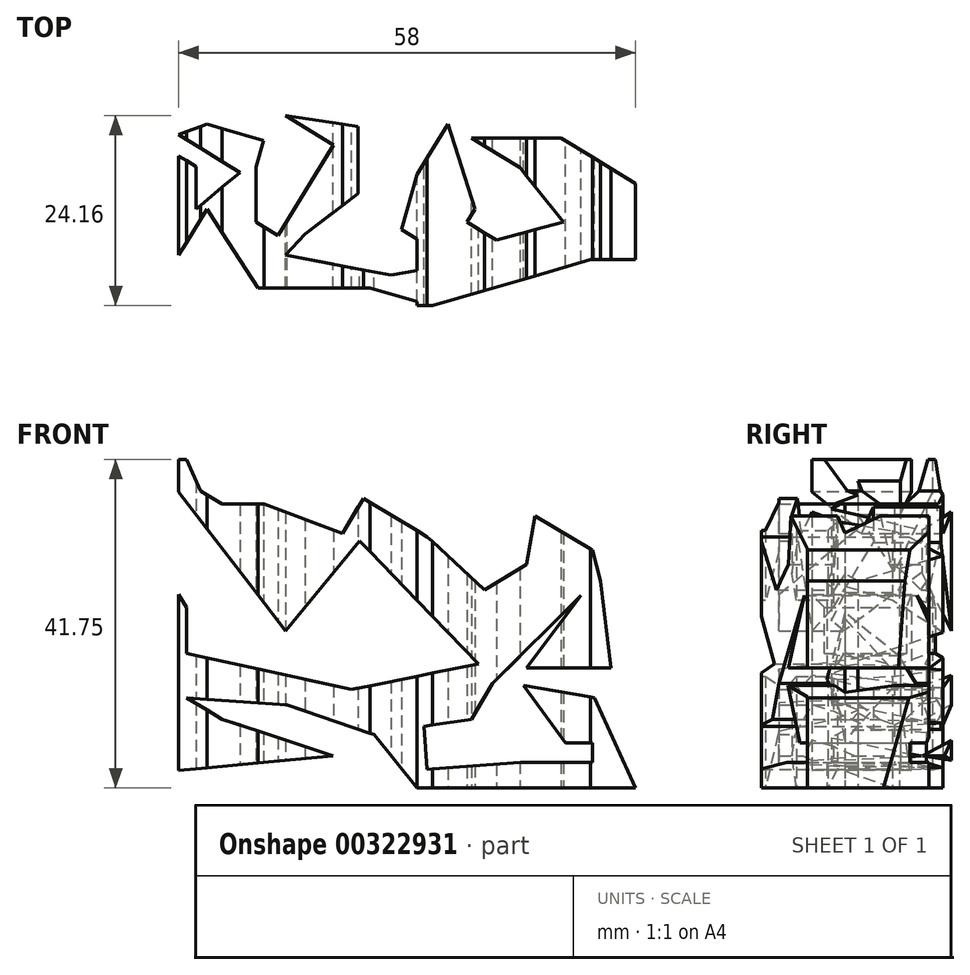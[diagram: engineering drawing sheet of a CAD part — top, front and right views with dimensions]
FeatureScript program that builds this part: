
annotation { "Feature Type Name" : "Feature", "Feature Type Description" : "" }
export const myFeature = defineFeature(function(context is Context, id is Id, definition is map)
    precondition{}
    {
        {
            var Q0;
            Q0=qCreatedBy(makeId("Front.planeOp"),FACE);
            var sketch = newSketch(context, id + "F0", { "sketchPlane" : qUnion([Q0])});
            skLineSegment(sketch, "E0.bottom", {"start": v(0, 0) * mm, "end": v(-66.39, 0) * mm});
            skLineSegment(sketch, "E0.top", {"start": v(0, -42.4) * mm, "end": v(-66.39, -42.4) * mm});
            skLineSegment(sketch, "E0.left", {"start": v(0, 0) * mm, "end": v(0, -42.4) * mm});
            skLineSegment(sketch, "E0.right", {"start": v(-66.39, 0) * mm, "end": v(-66.39, -42.4) * mm});
            skSolve(sketch);
        }
        {
            var Q0;
            Q0=makeQuery(id+"F0.imprint","IMPRINT",FACE,{"disambiguationData":[TD([[makeQuery(id+"F0.imprint","IMPRINT",EDGE,{"derivedFrom":sQuery(id+"F0.wireOp",EDGE,"E0.bottom")}),1.0]])]});
            extrude(context, id + "F1", {"entities" : qUnion([Q0]), "depth" : 25.4 * mm});
        }
        {
            var Q0;
            Q0=qCreatedBy(makeId("Front.planeOp"),FACE);
            var sketch = newSketch(context, id + "F2", { "sketchPlane" : qUnion([Q0])});
            skLineSegment(sketch, "E1", {"start": v(-63, 0) * mm, "end": v(-46.2, -21.83) * mm});
            skLineSegment(sketch, "E2", {"start": v(-46.2, -21.83) * mm, "end": v(-36.83, -10.37) * mm});
            skLineSegment(sketch, "E3", {"start": v(-36.83, -10.37) * mm, "end": v(-21.72, -26) * mm});
            skLineSegment(sketch, "E4", {"start": v(-21.72, -26) * mm, "end": v(-37.87, -29.25) * mm});
            skLineSegment(sketch, "E5", {"start": v(-37.87, -29.25) * mm, "end": v(-58.83, -24.69) * mm});
            skLineSegment(sketch, "E6", {"start": v(-58.83, -24.69) * mm, "end": v(-58.83, -18.83) * mm});
            skLineSegment(sketch, "E7", {"start": v(-58.83, -18.83) * mm, "end": v(-63.13, -11.54) * mm});
            skLineSegment(sketch, "E8", {"start": v(-63.13, -11.54) * mm, "end": v(-63.13, -18.83) * mm});
            skLineSegment(sketch, "E9", {"start": v(-63.13, -18.83) * mm, "end": v(-61.18, -39.66) * mm});
            skLineSegment(sketch, "E10", {"start": v(-61.18, -39.66) * mm, "end": v(-40.17, -37.7) * mm});
            skLineSegment(sketch, "E11", {"start": v(-40.17, -37.7) * mm, "end": v(-54.28, -33.02) * mm});
            skLineSegment(sketch, "E12", {"start": v(-54.28, -33.02) * mm, "end": v(-58.83, -30.29) * mm});
            skLineSegment(sketch, "E13", {"start": v(-58.83, -30.29) * mm, "end": v(-46.07, -31.2) * mm});
            skLineSegment(sketch, "E14", {"start": v(-46.07, -31.2) * mm, "end": v(-35, -34.98) * mm});
            skLineSegment(sketch, "E15", {"start": v(-35, -34.98) * mm, "end": v(-29.54, -41.75) * mm});
            skLineSegment(sketch, "E16", {"start": v(-29.54, -41.75) * mm, "end": v(-21.85, -41.75) * mm});
            skLineSegment(sketch, "E17", {"start": v(-21.85, -41.75) * mm, "end": v(-1.8, -41.75) * mm});
            skLineSegment(sketch, "E18", {"start": v(-1.8, -41.75) * mm, "end": v(-7, -30.29) * mm});
            skLineSegment(sketch, "E19", {"start": v(-7, -30.29) * mm, "end": v(-16, -28.73) * mm});
            skLineSegment(sketch, "E20", {"start": v(-16, -28.73) * mm, "end": v(-10.65, -36.02) * mm});
            skLineSegment(sketch, "E21", {"start": v(-10.65, -36.02) * mm, "end": v(-7.27, -36.02) * mm});
            skLineSegment(sketch, "E22", {"start": v(-7.27, -36.02) * mm, "end": v(-7.27, -38.5) * mm});
            skLineSegment(sketch, "E23", {"start": v(-7.27, -38.5) * mm, "end": v(-16.38, -38.5) * mm});
            skLineSegment(sketch, "E24", {"start": v(-16.38, -38.5) * mm, "end": v(-28.23, -39.4) * mm});
            skLineSegment(sketch, "E25", {"start": v(-28.23, -39.4) * mm, "end": v(-28.66, -33.92) * mm});
            skLineSegment(sketch, "E26", {"start": v(-28.66, -33.92) * mm, "end": v(-22.63, -33.02) * mm});
            skLineSegment(sketch, "E27", {"start": v(-22.63, -33.02) * mm, "end": v(-19.92, -28.5) * mm});
            skLineSegment(sketch, "E28", {"start": v(-19.92, -28.5) * mm, "end": v(-8.7, -17.27) * mm});
            skLineSegment(sketch, "E29", {"start": v(-8.7, -17.27) * mm, "end": v(-15.6, -26.51) * mm});
            skLineSegment(sketch, "E30", {"start": v(-15.6, -26.51) * mm, "end": v(-9.48, -26.51) * mm});
            skLineSegment(sketch, "E31", {"start": v(-9.48, -26.51) * mm, "end": v(-4.92, -26.51) * mm});
            skLineSegment(sketch, "E32", {"start": v(-4.92, -26.51) * mm, "end": v(-6.23, -15.44) * mm});
            skLineSegment(sketch, "E33", {"start": v(-6.23, -15.44) * mm, "end": v(-7.27, -11.54) * mm});
            skLineSegment(sketch, "E34", {"start": v(-7.27, -11.54) * mm, "end": v(-14.55, -7.17) * mm});
            skLineSegment(sketch, "E35", {"start": v(-14.55, -7.17) * mm, "end": v(-15.6, -13.36) * mm});
            skLineSegment(sketch, "E36", {"start": v(-15.6, -13.36) * mm, "end": v(-20.94, -16.62) * mm});
            skLineSegment(sketch, "E37", {"start": v(-20.94, -16.62) * mm, "end": v(-28.23, -9.84) * mm});
            skLineSegment(sketch, "E38", {"start": v(-28.23, -9.84) * mm, "end": v(-36.35, -4.97) * mm});
            skLineSegment(sketch, "E39", {"start": v(-36.35, -4.97) * mm, "end": v(-39, -9.4) * mm});
            skLineSegment(sketch, "E40", {"start": v(-39, -9.4) * mm, "end": v(-48.94, -5.68) * mm});
            skLineSegment(sketch, "E41", {"start": v(-48.94, -5.68) * mm, "end": v(-54.28, -5.68) * mm});
            skLineSegment(sketch, "E42", {"start": v(-54.28, -5.68) * mm, "end": v(-57.03, -4.02) * mm});
            skLineSegment(sketch, "E43", {"start": v(-57.03, -4.02) * mm, "end": v(-58.83, 0) * mm});
            skLineSegment(sketch, "E44", {"start": v(-58.83, 0) * mm, "end": v(-49.07, 6.82) * mm});
            skLineSegment(sketch, "E45", {"start": v(-49.07, 6.82) * mm, "end": v(4.32, 2.27) * mm});
            skLineSegment(sketch, "E46", {"start": v(4.32, 2.27) * mm, "end": v(4.32, -51.78) * mm});
            skLineSegment(sketch, "E47", {"start": v(4.32, -51.78) * mm, "end": v(-68.86, -47.87) * mm});
            skLineSegment(sketch, "E48", {"start": v(-68.86, -47.87) * mm, "end": v(-73.55, -26.51) * mm});
            skLineSegment(sketch, "E49", {"start": v(-73.55, -26.51) * mm, "end": v(-70.03, -3.33) * mm});
            skLineSegment(sketch, "E50", {"start": v(-70.03, -3.33) * mm, "end": v(-65.01, 5.03) * mm});
            skLineSegment(sketch, "E51", {"start": v(-65.01, 5.03) * mm, "end": v(-63, 0) * mm});
            skSolve(sketch);
        }
        {
            var Q0;
            Q0=makeQuery(id+"F2.imprint","IMPRINT",FACE,{"disambiguationData":[TD([[makeQuery(id+"F2.imprint","IMPRINT",EDGE,{"derivedFrom":sQuery(id+"F2.wireOp",EDGE,"E1")}),-1.0]])]});
            extrude(context, id + "F3", {"entities" : qUnion([Q0]), "operationType" : NewBodyOperationType.REMOVE, "depth" : 25.4 * mm});
        }
        {
            var Q0;
            Q0=makeQuery(id+"F3.boolean.opBoolean","COPY",FACE,{"derivedFrom":makeQuery(id+"F3.opExtrude","SWEPT_FACE",FACE,{"disambiguationData":[OSD([sQuery(id+"F2.wireOp",EDGE,"E16"),sQuery(id+"F2.wireOp",EDGE,"E17")])]})});
            var sketch = newSketch(context, id + "F4", { "sketchPlane" : qUnion([Q0])});
            skLineSegment(sketch, "E52", {"start": v(-7.47, 19.56) * mm, "end": v(-27.56, 25.4) * mm});
            skLineSegment(sketch, "E53", {"start": v(-27.56, 25.4) * mm, "end": v(-35.5, 23.16) * mm});
            skLineSegment(sketch, "E54", {"start": v(-35.5, 23.16) * mm, "end": v(-49.75, 23.16) * mm});
            skLineSegment(sketch, "E55", {"start": v(-49.75, 23.16) * mm, "end": v(-56.2, 13.1) * mm});
            skLineSegment(sketch, "E56", {"start": v(-56.2, 13.1) * mm, "end": v(-59.8, 18.96) * mm});
            skLineSegment(sketch, "E57", {"start": v(-59.8, 18.96) * mm, "end": v(-59.8, 13.1) * mm});
            skLineSegment(sketch, "E58", {"start": v(-59.8, 13.1) * mm, "end": v(-59.8, 6.36) * mm});
            skLineSegment(sketch, "E59", {"start": v(-59.8, 6.36) * mm, "end": v(-57.6, 7.72) * mm});
            skLineSegment(sketch, "E60", {"start": v(-57.6, 7.72) * mm, "end": v(-57.6, 13.1) * mm});
            skLineSegment(sketch, "E61", {"start": v(-57.6, 13.1) * mm, "end": v(-52, 8.46) * mm});
            skLineSegment(sketch, "E62", {"start": v(-52, 8.46) * mm, "end": v(-59.8, 3.66) * mm});
            skLineSegment(sketch, "E63", {"start": v(-59.8, 3.66) * mm, "end": v(-56.2, 2.31) * mm});
            skLineSegment(sketch, "E64", {"start": v(-56.2, 2.31) * mm, "end": v(-49, 4.41) * mm});
            skLineSegment(sketch, "E65", {"start": v(-49, 4.41) * mm, "end": v(-49.98, 7.75) * mm});
            skLineSegment(sketch, "E66", {"start": v(-49.98, 7.75) * mm, "end": v(-49.98, 14.76) * mm});
            skLineSegment(sketch, "E67", {"start": v(-49.98, 14.76) * mm, "end": v(-47.19, 16.48) * mm});
            skLineSegment(sketch, "E68", {"start": v(-47.19, 16.48) * mm, "end": v(-40.12, 4.99) * mm});
            skLineSegment(sketch, "E69", {"start": v(-40.12, 4.99) * mm, "end": v(-46.22, 1.24) * mm});
            skLineSegment(sketch, "E70", {"start": v(-46.22, 1.24) * mm, "end": v(-37, 2.61) * mm});
            skLineSegment(sketch, "E71", {"start": v(-37, 2.61) * mm, "end": v(-37, 11.16) * mm});
            skLineSegment(sketch, "E72", {"start": v(-37, 11.16) * mm, "end": v(-43.76, 16.26) * mm});
            skLineSegment(sketch, "E73", {"start": v(-43.76, 16.26) * mm, "end": v(-46.22, 18.96) * mm});
            skLineSegment(sketch, "E74", {"start": v(-46.22, 18.96) * mm, "end": v(-32.8, 21.5) * mm});
            skLineSegment(sketch, "E75", {"start": v(-32.8, 21.5) * mm, "end": v(-24.56, 20) * mm});
            skLineSegment(sketch, "E76", {"start": v(-24.56, 20) * mm, "end": v(-31.5, 15.74) * mm});
            skLineSegment(sketch, "E77", {"start": v(-31.5, 15.74) * mm, "end": v(-29.54, 8.76) * mm});
            skLineSegment(sketch, "E78", {"start": v(-29.54, 8.76) * mm, "end": v(-25.59, 2.34) * mm});
            skLineSegment(sketch, "E79", {"start": v(-25.59, 2.34) * mm, "end": v(-22.16, 13.1) * mm});
            skLineSegment(sketch, "E80", {"start": v(-22.16, 13.1) * mm, "end": v(-23.18, 14.76) * mm});
            skLineSegment(sketch, "E81", {"start": v(-23.18, 14.76) * mm, "end": v(-19.44, 17.06) * mm});
            skLineSegment(sketch, "E82", {"start": v(-19.44, 17.06) * mm, "end": v(-10.92, 14.76) * mm});
            skLineSegment(sketch, "E83", {"start": v(-10.92, 14.76) * mm, "end": v(-16.47, 7.86) * mm});
            skLineSegment(sketch, "E84", {"start": v(-16.47, 7.86) * mm, "end": v(-22.61, 4.08) * mm});
            skLineSegment(sketch, "E85", {"start": v(-22.61, 4.08) * mm, "end": v(-11.22, 4.08) * mm});
            skLineSegment(sketch, "E86", {"start": v(-11.22, 4.08) * mm, "end": v(-1.8, 9.87) * mm});
            skLineSegment(sketch, "E87", {"start": v(-7.47, 19.56) * mm, "end": v(-1.8, 19.56) * mm});
            skLineSegment(sketch, "E88", {"start": v(-1.8, 19.56) * mm, "end": v(6.77, 21.36) * mm});
            skLineSegment(sketch, "E89", {"start": v(6.77, 21.36) * mm, "end": v(-6.42, 42.8) * mm});
            skLineSegment(sketch, "E90", {"start": v(-6.42, 42.8) * mm, "end": v(-57.25, 37.55) * mm});
            skLineSegment(sketch, "E91", {"start": v(-57.25, 37.55) * mm, "end": v(-91.59, 32.45) * mm});
            skLineSegment(sketch, "E92", {"start": v(-91.59, 32.45) * mm, "end": v(-74.5, -16.58) * mm});
            skLineSegment(sketch, "E93", {"start": v(-74.5, -16.58) * mm, "end": v(13.82, -14.63) * mm});
            skLineSegment(sketch, "E94", {"start": v(13.82, -14.63) * mm, "end": v(6.77, 8.16) * mm});
            skLineSegment(sketch, "E95", {"start": v(6.77, 8.16) * mm, "end": v(-1.8, 9.87) * mm});
            skSolve(sketch);
        }
        {
            var Q0;
            {var subQ6=sQuery(id+"F4.wireOp",EDGE,"E54");Q0=makeQuery(id+"F4.imprint","IMPRINT",FACE,{"disambiguationData":[TD([[makeQuery(id+"F4.imprint","IMPRINT",EDGE,{"derivedFrom":subQ6}),-1.0]])]});}
            var Q1;
            {var subQ0=sQuery(id+"F4.wireOp",EDGE,"E52");Q1=makeQuery(id+"F4.imprint","IMPRINT",FACE,{"disambiguationData":[TD([[makeQuery(id+"F4.imprint","IMPRINT",EDGE,{"derivedFrom":subQ0}),-1.0]])]});}
            var Q2;
            {var subQ4=sQuery(id+"F4.wireOp",EDGE,"E78");Q2=makeQuery(id+"F4.imprint","IMPRINT",FACE,{"disambiguationData":[TD([[makeQuery(id+"F4.imprint","IMPRINT",EDGE,{"derivedFrom":subQ4}),-1.0]])]});}
            extrude(context, id + "F5", {"entities" : qUnion([Q0, Q1, Q2]), "operationType" : NewBodyOperationType.REMOVE, "oppositeDirection" : true, "depth" : 76.2 * mm});
        }
    });
